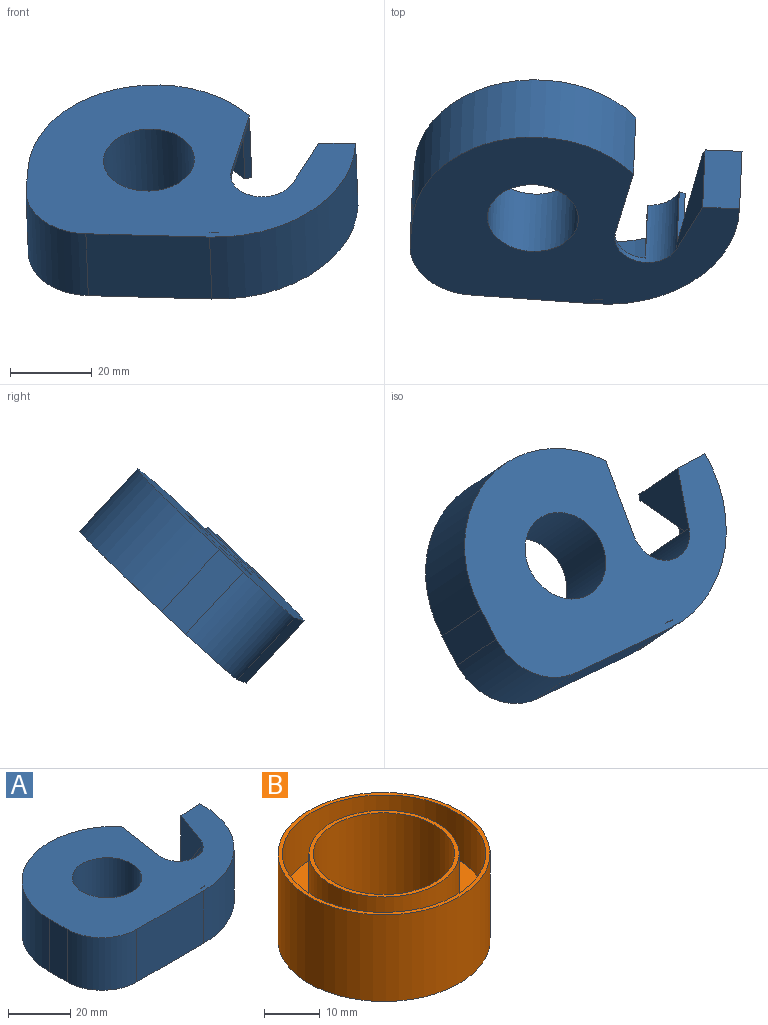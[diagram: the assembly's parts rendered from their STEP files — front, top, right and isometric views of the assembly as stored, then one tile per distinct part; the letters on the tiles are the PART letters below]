
ASSEMBLY  parts=2 mates=1
PART A: 30 faces, bbox 79.4x54x20.6 mm
  f0: plane 19.05x13.46mm, normal (0.94,-0.34,0), area 145.1mm2, adj f16,f18,f19,f25,f28
  f1: plane 8.86x6.79mm, normal (0,0,-1), area 16.8mm2, adj f13,f17,f18,f29
  f2: cylinder r=31.75mm len=2.18mm, axis (0,0,-1), area 3.5mm2, adj f3,f12,f15,f16
  f3: cylinder r=28.57mm len=20.64mm, axis (0,0,-1), area 2.4mm2, adj f2,f12,f15,f20,f25
  f4: plane 19.8x2.99mm, normal (0.99,-0.15,0), area 31.8mm2, adj f5,f13,f15,f16
  f5: cylinder r=30.16mm len=52.71mm, axis (0,0,-1), area 1503.2mm2, adj f4,f6,f15,f24,f25
  f6: plane 20.64x8.06mm, normal (-1,0,0), area 166.3mm2, adj f5,f7,f15,f25
  f7: cylinder r=15.76mm len=20.64mm, axis (0,0,-1), area 510.8mm2, adj f6,f8,f15,f25
  f8: plane 30.28x20.64mm, normal (0,-1,0), area 624.9mm2, adj f7,f9,f15,f25
  f9: cylinder r=33.34mm len=35mm, axis (0,0,-1), area 1115mm2, adj f8,f10,f15,f25
  f10: plane 20.64x9.02mm, normal (-0.05,1,0), area 186.3mm2, adj f9,f11,f15,f25
  f11: plane 20.64x14.45mm, normal (-0.94,0.34,0), area 189.6mm2, adj f10,f13,f15,f25,f28
  f12: plane 32.37x20.64mm, normal (0,1,0), area 619.9mm2, adj f2,f3,f15,f16,f21,f25
  f13: cylinder r=7.94mm len=20.64mm, axis (0,0,-1), area 219.8mm2, adj f1,f4,f11,f15,f16,f17,f29
  f14: cylinder r=11.11mm len=22.23mm, axis (0,0,-1), area 1440.9mm2, adj f15,f27
  f15: plane 79.38x53.98mm, normal (0,0,1), area 2510.1mm2, adj f2,f3,f4,f5,f6,f7,f8,f9
  f16: plane 76.2x50.8mm, normal (0,0,-1), area 2046.1mm2, adj f0,f2,f4,f12,f13,f17,f18,f19
  f17: plane 19.05x1.59mm, normal (-1,0,0), area 30.2mm2, adj f1,f13,f16,f18
  f18: cylinder r=9.53mm len=19.05mm, axis (0,0,1), area 219.7mm2, adj f0,f1,f16,f17,f29
  f19: plane 19.05x6.34mm, normal (0.05,-1,0), area 121mm2, adj f0,f16,f20,f25
  f20: cylinder r=31.75mm len=31.68mm, axis (0,0,1), area 908.6mm2, adj f3,f16,f19,f25
  f21: cylinder r=14.17mm len=19.05mm, axis (0,0,1), area 424mm2, adj f12,f16,f22,f25
  f22: plane 19.05x8.06mm, normal (1,0,0), area 153.5mm2, adj f16,f21,f23,f25
  f23: cylinder r=28.57mm len=49.44mm, axis (0,0,1), area 1300.5mm2, adj f16,f22,f24,f25
  f24: plane 19.05x1.68mm, normal (0.29,-0.96,0), area 33.5mm2, adj f5,f16,f23,f25
  f25: plane 79.38x53.98mm, normal (0,0,-1), area 306.3mm2, adj f0,f3,f5,f6,f7,f8,f9,f10
  f26: cylinder r=12.7mm len=25.4mm, axis (0,0,1), area 1520.1mm2, adj f16,f27
  f27: plane 25.4x25.4mm, normal (0,0,-1), area 118.8mm2, adj f14,f26
  f28: plane 18.39x13.61mm, normal (-0.27,-0.75,-0.6), area 36.6mm2, adj f0,f11,f25,f29
  f29: plane 18.39x1.49mm, normal (0.34,0.94,0), area 29.2mm2, adj f1,f13,f18,f28
PART B: 8 faces, bbox 38.1x38.1x19.1 mm
  f0: plane 36.51x36.51mm, normal (0,0,1), area 475mm2, adj f4,f6
  f1: cylinder r=12.7mm len=25.4mm, axis (0,0,-1), area 1520.1mm2, adj f3,f7
  f2: cylinder r=19.05mm len=38.1mm, axis (0,0,-1), area 2280.2mm2, adj f3,f5
  f3: plane 38.1x38.1mm, normal (0,0,-1), area 633.4mm2, adj f1,f2
  f4: cylinder r=18.26mm len=36.51mm, axis (0,0,-1), area 1165.4mm2, adj f0,f5
  f5: plane 38.1x38.1mm, normal (0,0,1), area 93mm2, adj f2,f4
  f6: cylinder r=13.49mm len=26.99mm, axis (0,0,-1), area 861.4mm2, adj f0,f7
  f7: plane 26.99x26.99mm, normal (0,0,1), area 65.3mm2, adj f1,f6
PLACE A rot(axis=(0.99,0,-0.1),43.1deg) t=(-67.09,33.83,-95.81)mm
PLACE B rot(axis=(-0.98,-0.18,-0.09),138.3deg) t=(-75.67,53.1,-78.25)mm
MATE revolute B.f2 <-> A.f14  axis (-0.03,-0.68,0.73) through (-75.67,53.1,-78.25)mm
